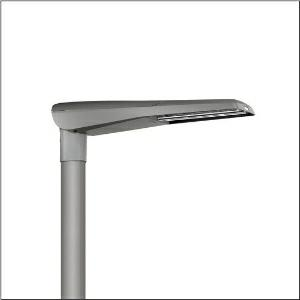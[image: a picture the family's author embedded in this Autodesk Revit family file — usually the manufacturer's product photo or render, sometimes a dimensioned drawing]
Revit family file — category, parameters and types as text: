
# Revit family: streetlight_sl_11_iq_mini___st1_2p1_0_5xc2gc1f08he_badf
name_source: partatom
category: Lighting Fixtures
units: mm (PartAtom-declared; Revit-internal decimal feet)

## family parameters
Cut with Voids When Loaded = No
Host = Face
Light Source = No
Part Type = Normal
Room Calculation Point = No
Round Connector Dimension = Use Diameter
Shared = No

## types (1)
- --- (1 x LED, 6750 lm, 63 W, 2200K)
    Apparent Load = 63 VA
    CIE Flux Codes = 31 68 95 100 100
    Color Rendering = 70
    Color Temperature = 2200K
    Default Elevation = 1800 mm
    Description = Streetlight SL 11 iQ mini, mast luminaire, primary light control with 3 zone facetted reflector, of plastic, silver coated, highly specular, primary optical cover: cover, of PMMA, transparent, light distribution: ST1.2P1.0, light emission: direct distribution, primary light characteristic: asymmetric, installation type: post-top, side-entry, lamps: LED, High Power LED, rated values: 8.240lm | 61,5W | 134lm/W (begin service life); end service life: 8.240lm | 64,5W; at 50% lumin. flux: 4.120lm | 29,1W | 141,6lm/W, colour temperature: 2200/2700/3000/4000K, colour rendering: CRI > 70, light colour: 722/727/730/740, light setting 1 begin service life: 100% | 8.240lm | 61,5W | 134lm/W | 3.000K, light setting 1 end service life: 64,5W, further light settings possible, control: Street-Remote, Auto-Match, Temp-Guard, Lumen-Switch, Night-Set, Smart-Wire, Light-Fading, Desk-Remote (wireless, voltage-free reading and setting of iQ features in the workshop via application-optimized NFC function/RFID function), optimised constant luminous flux control (CLO 2.0), with cable H07RN-F 3x 1.5mm², mains connection: 230..240V, AC, 50/60Hz, connection cable pre-assembled, cable length: 8,5m, luminaire housing, of diecast aluminium, powder-coated, SITECO metallic grey (DB 702S), please order mast flange separately, inclination adjustable without tools: 0°, 5°, 10°, 15° (post-top) | 0°, -5°, -10°, -15° (side-entry), sealing non-destructively replaceable, multi-level sealing system, length: 736mm, width: 174mm, height: 116mm, mast flange for spigot size: 42mm (side-entry): 5XC10008XM4, 60/48mm (side-entry/post-top): 5XC10108XM2, 76/60mm (side-entry/post-top): 5XC10108XM1, equipment: Power, protection rating (complete): IP66, insulation class (complete): insulation class II (safety insulation), certification: CE, ENEC, ENEC+, VDE, impact resistance: IK10, permissible operating ambient temperature for outdoor applications: -25..+50°C, standard-compliant lighting for roads and squares, Environmental Product Declaration (EPD) tested and certified by an independent institute, packaging unit: 1 piece

Light Distribution: ST1.2P1.0
    Height = 116 mm
    Lamp = 1 x LED
    Lamp Light Flux = 6750 lm
    Lamp Power = 63 W
    Lamp count = 1
    Length = 736 mm
    Luminous efficacy = 107 lm/W
    Manufacturer = Siteco
    ModVariant = No
    Model = 5XC2GC1F08HE
    Number of Poles = 1
    OnlyDefault = Yes
    Power Factor = 1
    Product Name = Streetlight SL 11 iQ mini | ST1.2P1.0
    Product group = mast luminaire | pylon top
    ProductGroupID = 6100
    Protection Class = Protection class II
    Protection Degree = IP 66
    RLX_Detail_Level = 1
    RLX_Emergency_Light_Flux = 0 lm
    RLX_Emergency_Type = 0
    RLX_Emergency_Type_DB = No
    RlxData = <blob elided: 53693 chars, md5=339162aa>
    Socket = socket
    Standby Power = 0 W
    System Light Flux = 6750 lm
    System Power = 63 W
    Type Comments = individual setting: luminous flux: 100 % | dim-lin: 254 | 858 mA
    Type Image = l_1003508.jpg
    URL = http://relux.com
    VarID = @adj_041401
    Voltage = 0 V
    Weight = 0.00 kg
    Width = 174 mm

## geometry (parser evidence)
native form markers: Blend x4, Sweep x10
no freeform markers — native parametric forms only
